# Revit family: ASH_Contour21_S6452_BIM_GB
name_source: partatom
category: Plumbing Fixtures
revit_build: Autodesk Revit MEP 2012 (Build: 20110309_2315(x64)
units: mm (PartAtom-declared; Revit-internal decimal feet)

## types (5) — shared parameters
AccessibilityPerformance = DDA Compliant
Accessories = www.idealspec.co.uk
Assembly Code = C1030200
AssetType = Fixed
BIMObjectName = GRABRAIL_ArmitageShanks_Contour21-Straight45cm_S6452
Brand = Armitage Shanks
Category = Furniture_GRABRAIL_UK
ConnectionType = Mechanical
CurrentRevision = 1
Default Elevation = 1219 mm
Description = Contour 21 grab rail straight 45cm long x 35mm diameter
DurationUnit = Years
ElementType = GRAB RAIL: Safety device to aid maintaining balance, lessen fatigue and assist in supporting weight whilst maneuvering the body
ExpectedLife = 30
Help = http://www.idealspec.co.uk
InstallationInstructions = http://www.idealspec.co.uk
Manufacturer = Ideal Standard International Ltd
ManufacturerURL = www.idealspec.co.uk
Name = GRABRAIL_ArmitageShanks_Contour21-Straight45cm_S6452
NettWeight = 0.62Kg
NominalHeight = 118 mm
NominalLength = 450 mm  [stored 1.47638 ft]
NominalWidth = 84 mm
PredefinedType = grabrail
ProductDataSheet = http://www.idealspec.co.uk
ProductInformation = http://www.idealspec.co.uk
SalesInformation = http://www.idealspec.co.uk
SendEnquiry = http://www.idealspec.co.uk
Shape = Tubular
Size = mm x mm x mm
Space = Internal
SpareParts = www.fastpart-spares.co.uk
StandardsConformance = DDA, Doc-M
URL = www.idealspec.co.uk
Version = 2
VolumeUnits = Litres
WarrantyDescription = Manufacturers Warranty
WarrantyDurationParts = 5
WarrantyDurationUnit = Years
WarrantyGuarantorParts = Ideal Standard International Ltd

## per-type parameters (varying)
| type | BREEAM Approved | BarCode | Colour | ECA | Features | Finish | Grade | LRVValue | Material | Model | ModelNumber | ModelReference | RAL | WRAS | WaterEfficientProduct |
| S6452LI | No | 5017830384861 | Powder Coated Aluminium Blue LI | No | straight 45cm long x 35mm diameter Blue | Powder Coated Aluminium Blue LI | T6 | 27 | Aluminium | S645236 | S645236 | S645236 | 5011 | No | No |
| S645201 | No | 5017830383758 | Powder Coated Aluminium White 01 | No | Straight 45cm Long x 35mm diameter | Powder Coated Aluminium White 01 | T6 | 94 | Alumnium | S6452AC | S6452AC | S6452AC | 9016 | No | No |
| S6452LJ | No | 5017830384540 | Powder Coated Aluminium Grey LJ | No | straight 45cm long x 35mm diameter Light Grey | Powder Coated Aluminium Grey LJ | T6 | 20 | Aluminium | S6452LJ | S6452LJ | S6452LJ | 7005 | No | No |
| S6452RN | Yes | 5017830388401 | Powder Coated Aluminium Charcoal RN | Yes | straight 45cm long x 35mm diameter Charcoal | Powder Coated Aluminium Charcoal RN | T6 | 9 | Aluminium | S6452RN | S6452RN | S6452RN | 7016 | Yes | Yes |
| S6452MY | No | 5017830384229 | Stainless Steel MY | No | straight 45cm long x 35mm diameter Stainless Steel | Polished | 304 |  | Stainless Steel | S6452MY | S6452MY | S6452MY |  | No | No |

note: column(s) folded — value = type name in every type: PartNumber

note: [stored X ft] marks values corroborated as IEEE doubles in the binary element streams (Revit-internal decimal feet)

## geometry (parser evidence)
native form markers: Blend x9, Sweep x3
no freeform markers — native parametric forms only
